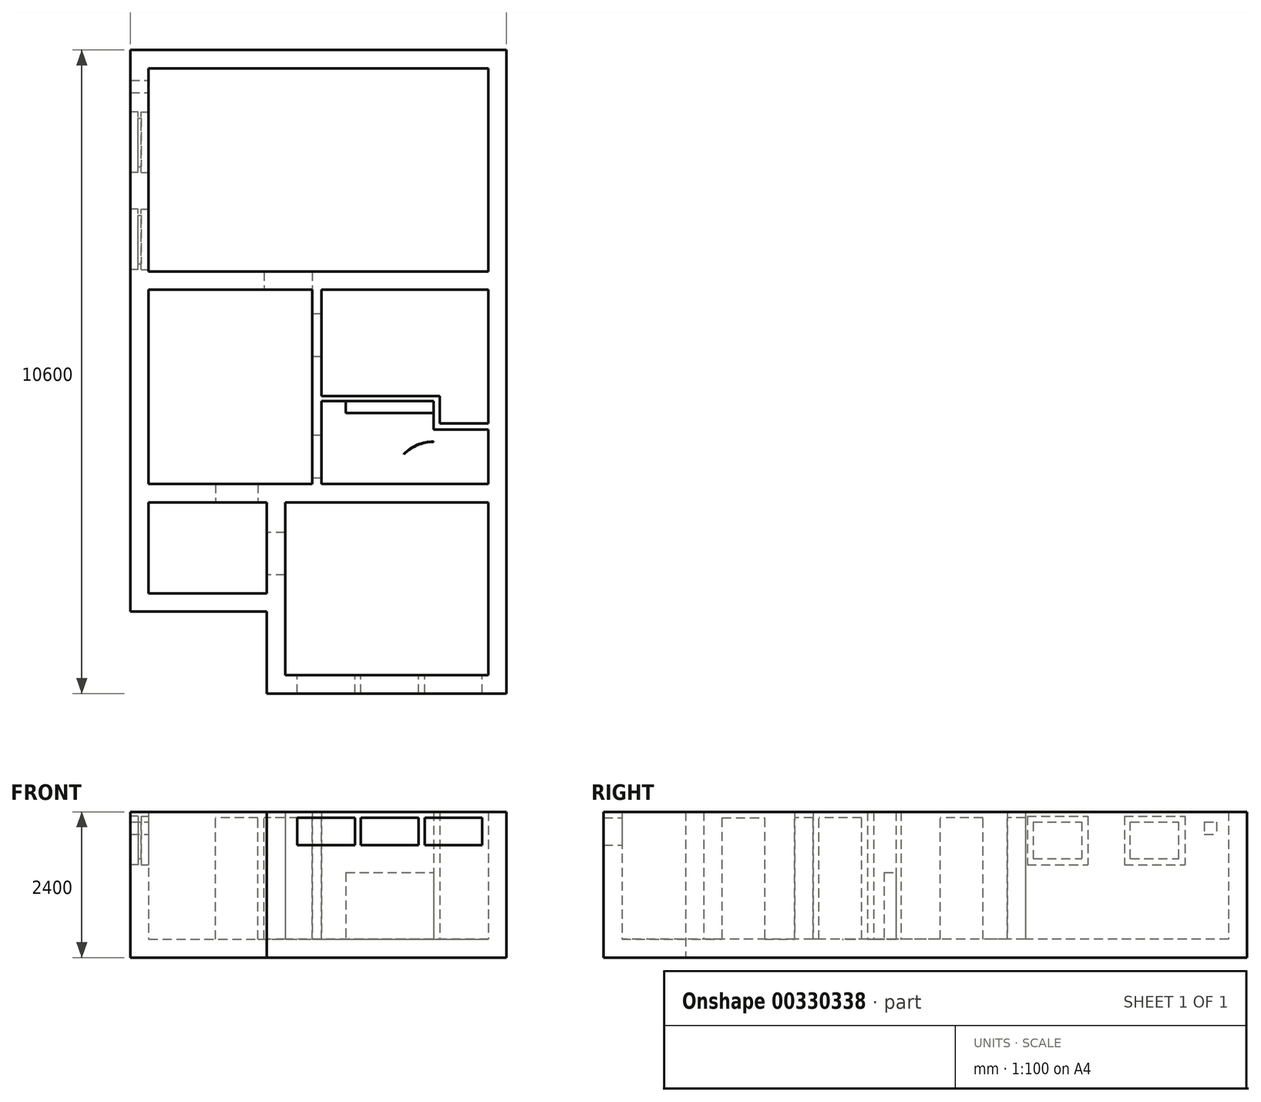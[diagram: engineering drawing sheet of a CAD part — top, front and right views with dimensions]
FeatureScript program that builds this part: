
annotation { "Feature Type Name" : "Feature", "Feature Type Description" : "" }
export const myFeature = defineFeature(function(context is Context, id is Id, definition is map)
    precondition{}
    {
        {
            var Q0;
            Q0=qCreatedBy(makeId("Top.planeOp"),FACE);
            var sketch = newSketch(context, id + "F0", { "sketchPlane" : qUnion([Q0])});
            skLineSegment(sketch, "E0.bottom", {"start": v(0, 0) * mm, "end": v(5600, 0) * mm});
            skLineSegment(sketch, "E0.top", {"start": v(0, -8650) * mm, "end": v(1950, -8650) * mm});
            skLineSegment(sketch, "E0.left", {"start": v(0, 0) * mm, "end": v(0, -3350) * mm});
            skLineSegment(sketch, "E0.right", {"start": v(5600, 0) * mm, "end": v(5600, -3350) * mm});
            skLineSegment(sketch, "E1", {"start": v(0, -3650) * mm, "end": v(2700, -3650) * mm});
            skLineSegment(sketch, "E2", {"start": v(5600, -8650) * mm, "end": v(5600, -10000) * mm});
            skLineSegment(sketch, "E3", {"start": v(5600, -10000) * mm, "end": v(2250, -10000) * mm});
            skLineSegment(sketch, "E4", {"start": v(2250, -10000) * mm, "end": v(2250, -8650) * mm});
            skLineSegment(sketch, "E5", {"start": v(0, -7150) * mm, "end": v(1950, -7150) * mm});
            skLineSegment(sketch, "E6", {"start": v(2250, -8650) * mm, "end": v(2250, -7150) * mm});
            skLineSegment(sketch, "E7", {"start": v(0, -3350) * mm, "end": v(5600, -3350) * mm});
            skLineSegment(sketch, "E8", {"start": v(0, -6850) * mm, "end": v(2700, -6850) * mm});
            skLineSegment(sketch, "E9", {"start": v(1950, -7150) * mm, "end": v(1950, -8650) * mm});
            skLineSegment(sketch, "E10.bottom", {"start": v(5900, 300) * mm, "end": v(-300, 300) * mm});
            skLineSegment(sketch, "E10.top", {"start": v(5900, -10300) * mm, "end": v(1950, -10300) * mm});
            skLineSegment(sketch, "E10.left", {"start": v(5900, 300) * mm, "end": v(5900, -10300) * mm});
            skLineSegment(sketch, "E10.right", {"start": v(-300, 300) * mm, "end": v(-300, -8950) * mm});
            skLineSegment(sketch, "E11", {"start": v(-300, -8950) * mm, "end": v(1950, -8950) * mm});
            skLineSegment(sketch, "E12", {"start": v(1950, -8950) * mm, "end": v(1950, -10300) * mm});
            skLineSegment(sketch, "E13", {"start": v(2700, -3650) * mm, "end": v(2700, -6850) * mm});
            skLineSegment(sketch, "E14.trimOffspring", {"start": v(0, -3650) * mm, "end": v(0, -6850) * mm});
            skLineSegment(sketch, "E15.trimOffspring", {"start": v(2850, -3650) * mm, "end": v(5600, -3650) * mm});
            skLineSegment(sketch, "E16.trimOffspring", {"start": v(2850, -6850) * mm, "end": v(5600, -6850) * mm});
            skLineSegment(sketch, "E17.trimOffspring", {"start": v(2250, -7150) * mm, "end": v(5600, -7150) * mm});
            skLineSegment(sketch, "E18.trimOffspring", {"start": v(5600, -7150) * mm, "end": v(5600, -8650) * mm});
            skLineSegment(sketch, "E19.trimOffspring", {"start": v(0, -7150) * mm, "end": v(0, -8650) * mm});
            skLineSegment(sketch, "E20", {"start": v(5600, -3650) * mm, "end": v(5600, -5850) * mm});
            skLineSegment(sketch, "E21", {"start": v(2850, -3650) * mm, "end": v(2850, -5400) * mm});
            skLineSegment(sketch, "E22.bottom", {"start": v(5600, -5850) * mm, "end": v(4800, -5850) * mm});
            skLineSegment(sketch, "E22.top", {"start": v(5600, -5950) * mm, "end": v(4700, -5950) * mm});
            skLineSegment(sketch, "E23.trimOffspring", {"start": v(2850, -5480) * mm, "end": v(2850, -6850) * mm});
            skLineSegment(sketch, "E24.trimOffspring", {"start": v(5600, -5950) * mm, "end": v(5600, -6850) * mm});
            skLineSegment(sketch, "E25.top", {"start": v(2850, -5400) * mm, "end": v(4800, -5400) * mm});
            skLineSegment(sketch, "E26.top", {"start": v(2850, -5480) * mm, "end": v(4700, -5480) * mm});
            skLineSegment(sketch, "E26.right", {"start": v(4700, -5950) * mm, "end": v(4700, -5480) * mm});
            skLineSegment(sketch, "E27.right", {"start": v(4800, -5850) * mm, "end": v(4800, -5400) * mm});
            skSolve(sketch);
        }
        {
            var Q0;
            Q0=qSketchRegion(id+"F0",true);
            extrude(context, id + "F1", {"entities" : qUnion([Q0]), "depth" : 2100 * mm});
        }
        {
            var Q0;
            Q0=makeQuery(id+"F0.imprint","IMPRINT",FACE,{"disambiguationData":[TD([[makeQuery(id+"F0.imprint","IMPRINT",EDGE,{"derivedFrom":sQuery(id+"F0.wireOp",EDGE,"E0.bottom")}),1.0]])]});
            var sketch = newSketch(context, id + "F2", { "sketchPlane" : qUnion([Q0])});
            skLineSegment(sketch, "E28.0", {"start": v(-300, -8950) * mm, "end": v(1950, -8950) * mm});
            skLineSegment(sketch, "E29.0", {"start": v(-300, 300) * mm, "end": v(-300, -8950) * mm});
            skLineSegment(sketch, "E30.0", {"start": v(5900, 300) * mm, "end": v(-300, 300) * mm});
            skLineSegment(sketch, "E31.0", {"start": v(5900, 300) * mm, "end": v(5900, -10300) * mm});
            skLineSegment(sketch, "E32.0", {"start": v(5900, -10300) * mm, "end": v(1950, -10300) * mm});
            skLineSegment(sketch, "E33.0", {"start": v(1950, -8950) * mm, "end": v(1950, -10300) * mm});
            skSolve(sketch);
        }
        {
            var Q0;
            Q0=qSketchRegion(id+"F2",true);
            extrude(context, id + "F3", {"entities" : qUnion([Q0]), "operationType" : NewBodyOperationType.ADD, "oppositeDirection" : true, "depth" : 300 * mm});
        }
        {
            var Q0;
            Q0=makeQuery(id+"F1.opExtrude","SWEPT_FACE",FACE,{"disambiguationData":[OSD([sQuery(id+"F0.wireOp",EDGE,"E3")])]});
            var sketch = newSketch(context, id + "F4", { "sketchPlane" : qUnion([Q0])});
            skLineSegment(sketch, "E34.bottom", {"start": v(-5500, 2000) * mm, "end": v(-4550, 2000) * mm});
            skLineSegment(sketch, "E34.top", {"start": v(-5500, 1550) * mm, "end": v(-4550, 1550) * mm});
            skLineSegment(sketch, "E34.left", {"start": v(-5500, 2000) * mm, "end": v(-5500, 1550) * mm});
            skLineSegment(sketch, "E34.right", {"start": v(-4550, 2000) * mm, "end": v(-4550, 1550) * mm});
            skLineSegment(sketch, "E35.bottom", {"start": v(-4450, 2000) * mm, "end": v(-3500, 2000) * mm});
            skLineSegment(sketch, "E35.top", {"start": v(-4450, 1550) * mm, "end": v(-3500, 1550) * mm});
            skLineSegment(sketch, "E35.left", {"start": v(-4450, 2000) * mm, "end": v(-4450, 1550) * mm});
            skLineSegment(sketch, "E35.right", {"start": v(-3500, 2000) * mm, "end": v(-3500, 1550) * mm});
            skLineSegment(sketch, "E36.bottom", {"start": v(-3400, 2000) * mm, "end": v(-2450, 2000) * mm});
            skLineSegment(sketch, "E36.top", {"start": v(-3400, 1550) * mm, "end": v(-2450, 1550) * mm});
            skLineSegment(sketch, "E36.left", {"start": v(-3400, 2000) * mm, "end": v(-3400, 1550) * mm});
            skLineSegment(sketch, "E36.right", {"start": v(-2450, 2000) * mm, "end": v(-2450, 1550) * mm});
            skSolve(sketch);
        }
        {
            var Q0;
            Q0=qSketchRegion(id+"F4",true);
            extrude(context, id + "F5", {"entities" : qUnion([Q0]), "operationType" : NewBodyOperationType.REMOVE, "endBound" : BoundingType.UP_TO_NEXT, "oppositeDirection" : true, "depth" : 25 * mm});
        }
        {
            var Q0;
            Q0=makeQuery(id+"F1.opExtrude","SWEPT_FACE",FACE,{"disambiguationData":[OSD([sQuery(id+"F0.wireOp",EDGE,"E5")])]});
            var sketch = newSketch(context, id + "F6", { "sketchPlane" : qUnion([Q0])});
            skLineSegment(sketch, "E37.bottom", {"start": v(1800, 0) * mm, "end": v(1100, 0) * mm});
            skLineSegment(sketch, "E37.top", {"start": v(1800, 2000) * mm, "end": v(1100, 2000) * mm});
            skLineSegment(sketch, "E37.left", {"start": v(1800, 0) * mm, "end": v(1800, 2000) * mm});
            skLineSegment(sketch, "E37.right", {"start": v(1100, 0) * mm, "end": v(1100, 2000) * mm});
            skSolve(sketch);
        }
        {
            var Q0;
            Q0=qSketchRegion(id+"F6",true);
            extrude(context, id + "F7", {"entities" : qUnion([Q0]), "operationType" : NewBodyOperationType.REMOVE, "endBound" : BoundingType.UP_TO_NEXT, "oppositeDirection" : true, "depth" : 25 * mm});
        }
        {
            var Q0;
            Q0=makeQuery(id+"F1.opExtrude","SWEPT_FACE",FACE,{"disambiguationData":[OSD([sQuery(id+"F0.wireOp",EDGE,"E9")])]});
            var sketch = newSketch(context, id + "F8", { "sketchPlane" : qUnion([Q0])});
            skLineSegment(sketch, "E38.bottom", {"start": v(7650, 0) * mm, "end": v(8350, 0) * mm});
            skLineSegment(sketch, "E38.top", {"start": v(7650, 2000) * mm, "end": v(8350, 2000) * mm});
            skLineSegment(sketch, "E38.left", {"start": v(7650, 0) * mm, "end": v(7650, 2000) * mm});
            skLineSegment(sketch, "E38.right", {"start": v(8350, 0) * mm, "end": v(8350, 2000) * mm});
            skSolve(sketch);
        }
        {
            var Q0;
            Q0=qSketchRegion(id+"F8",true);
            extrude(context, id + "F9", {"entities" : qUnion([Q0]), "operationType" : NewBodyOperationType.REMOVE, "endBound" : BoundingType.UP_TO_NEXT, "oppositeDirection" : true, "depth" : 25 * mm});
        }
        {
            var Q0;
            Q0=makeQuery(id+"F1.opExtrude","SWEPT_FACE",FACE,{"disambiguationData":[OSD([sQuery(id+"F0.wireOp",EDGE,"E1")])]});
            var sketch = newSketch(context, id + "F10", { "sketchPlane" : qUnion([Q0])});
            skLineSegment(sketch, "E39.bottom", {"start": v(2700, 0) * mm, "end": v(1900, 0) * mm});
            skLineSegment(sketch, "E39.top", {"start": v(2700, 2000) * mm, "end": v(1900, 2000) * mm});
            skLineSegment(sketch, "E39.left", {"start": v(2700, 0) * mm, "end": v(2700, 2000) * mm});
            skLineSegment(sketch, "E39.right", {"start": v(1900, 0) * mm, "end": v(1900, 2000) * mm});
            skSolve(sketch);
        }
        {
            var Q0;
            Q0=qSketchRegion(id+"F10",true);
            extrude(context, id + "F11", {"entities" : qUnion([Q0]), "operationType" : NewBodyOperationType.REMOVE, "endBound" : BoundingType.UP_TO_NEXT, "oppositeDirection" : true, "depth" : 25 * mm});
        }
        {
            var Q0;
            Q0=makeQuery(id+"F1.opExtrude","SWEPT_FACE",FACE,{"disambiguationData":[OSD([sQuery(id+"F0.wireOp",EDGE,"E13")])]});
            var sketch = newSketch(context, id + "F12", { "sketchPlane" : qUnion([Q0])});
            skLineSegment(sketch, "E40.bottom", {"start": v(6050, 0) * mm, "end": v(6750, 0) * mm});
            skLineSegment(sketch, "E40.top", {"start": v(6050, 2000) * mm, "end": v(6750, 2000) * mm});
            skLineSegment(sketch, "E40.left", {"start": v(6050, 0) * mm, "end": v(6050, 2000) * mm});
            skLineSegment(sketch, "E40.right", {"start": v(6750, 0) * mm, "end": v(6750, 2000) * mm});
            skLineSegment(sketch, "E41.bottom", {"start": v(4050, 0) * mm, "end": v(4750, 0) * mm});
            skLineSegment(sketch, "E41.top", {"start": v(4050, 2000) * mm, "end": v(4750, 2000) * mm});
            skLineSegment(sketch, "E41.left", {"start": v(4050, 0) * mm, "end": v(4050, 2000) * mm});
            skLineSegment(sketch, "E41.right", {"start": v(4750, 0) * mm, "end": v(4750, 2000) * mm});
            skSolve(sketch);
        }
        {
            var Q0;
            Q0=qSketchRegion(id+"F12",true);
            extrude(context, id + "F13", {"entities" : qUnion([Q0]), "operationType" : NewBodyOperationType.REMOVE, "endBound" : BoundingType.UP_TO_NEXT, "oppositeDirection" : true, "depth" : 25 * mm});
        }
        {
            var Q0;
            Q0=makeQuery(id+"F1.opExtrude","SWEPT_FACE",FACE,{"disambiguationData":[OSD([sQuery(id+"F0.wireOp",EDGE,"E0.left")])]});
            var sketch = newSketch(context, id + "F14", { "sketchPlane" : qUnion([Q0])});
            skLineSegment(sketch, "E42.bottom", {"start": v(-3220, 1930) * mm, "end": v(-2420, 1930) * mm});
            skLineSegment(sketch, "E42.top", {"start": v(-3220, 1730) * mm, "end": v(-2420, 1730) * mm});
            skLineSegment(sketch, "E42.left", {"start": v(-3220, 1930) * mm, "end": v(-3220, 1730) * mm});
            skLineSegment(sketch, "E42.right", {"start": v(-2420, 1930) * mm, "end": v(-2420, 1730) * mm});
            skLineSegment(sketch, "E43.bottom", {"start": v(-400, 1930) * mm, "end": v(-200, 1930) * mm});
            skLineSegment(sketch, "E43.top", {"start": v(-400, 1730) * mm, "end": v(-200, 1730) * mm});
            skLineSegment(sketch, "E43.left", {"start": v(-400, 1930) * mm, "end": v(-400, 1730) * mm});
            skLineSegment(sketch, "E43.right", {"start": v(-200, 1930) * mm, "end": v(-200, 1730) * mm});
            skSolve(sketch);
        }
        {
            var Q0;
            Q0 = qSketchRegion(id + "F14", true);
            extrude(context, id + "F15", {"entities" : qUnion([Q0]), "operationType" : NewBodyOperationType.REMOVE, "endBound" : BoundingType.THROUGH_ALL, "oppositeDirection" : true, "depth" : 25 * mm});
        }
        {
            var Q0;
            Q0=makeQuery(id+"F1.opExtrude","SWEPT_FACE",FACE,{"disambiguationData":[OSD([sQuery(id+"F0.wireOp",EDGE,"E0.left")])]});
            var sketch = newSketch(context, id + "F16", { "sketchPlane" : qUnion([Q0])});
            skLineSegment(sketch, "E44.bottom", {"start": v(-3220, 1930) * mm, "end": v(-2420, 1930) * mm});
            skLineSegment(sketch, "E44.top", {"start": v(-3220, 1330) * mm, "end": v(-2420, 1330) * mm});
            skLineSegment(sketch, "E44.left", {"start": v(-3220, 1930) * mm, "end": v(-3220, 1330) * mm});
            skLineSegment(sketch, "E44.right", {"start": v(-2420, 1930) * mm, "end": v(-2420, 1330) * mm});
            skLineSegment(sketch, "E45.bottom", {"start": v(-1620, 1330) * mm, "end": v(-820, 1330) * mm});
            skLineSegment(sketch, "E45.top", {"start": v(-1620, 1930) * mm, "end": v(-820, 1930) * mm});
            skLineSegment(sketch, "E45.left", {"start": v(-1620, 1330) * mm, "end": v(-1620, 1930) * mm});
            skLineSegment(sketch, "E45.right", {"start": v(-820, 1330) * mm, "end": v(-820, 1930) * mm});
            skLineSegment(sketch, "E46.bottom", {"start": v(-400, 1930) * mm, "end": v(-200, 1930) * mm});
            skLineSegment(sketch, "E46.top", {"start": v(-400, 1730) * mm, "end": v(-200, 1730) * mm});
            skLineSegment(sketch, "E46.left", {"start": v(-400, 1930) * mm, "end": v(-400, 1730) * mm});
            skLineSegment(sketch, "E46.right", {"start": v(-200, 1930) * mm, "end": v(-200, 1730) * mm});
            skSolve(sketch);
        }
        {
            var Q0;
            Q0 = qSketchRegion(id + "F16", true);
            extrude(context, id + "F17", {"entities" : qUnion([Q0]), "operationType" : NewBodyOperationType.REMOVE, "endBound" : BoundingType.THROUGH_ALL, "oppositeDirection" : true, "depth" : 25 * mm});
        }
        {
            var Q0;
            Q0=makeQuery(id+"F1.opExtrude","SWEPT_FACE",FACE,{"disambiguationData":[OSD([sQuery(id+"F0.wireOp",EDGE,"E0.left")])]});
            var sketch = newSketch(context, id + "F18", { "sketchPlane" : qUnion([Q0])});
            skLineSegment(sketch, "E47.bottom", {"start": v(-3320, 2030) * mm, "end": v(-2320, 2030) * mm});
            skLineSegment(sketch, "E47.top", {"start": v(-3320, 1230) * mm, "end": v(-2320, 1230) * mm});
            skLineSegment(sketch, "E47.left", {"start": v(-3320, 2030) * mm, "end": v(-3320, 1230) * mm});
            skLineSegment(sketch, "E47.right", {"start": v(-2320, 2030) * mm, "end": v(-2320, 1230) * mm});
            skLineSegment(sketch, "E48.bottom", {"start": v(-1720, 2030) * mm, "end": v(-720, 2030) * mm});
            skLineSegment(sketch, "E48.top", {"start": v(-1720, 1230) * mm, "end": v(-720, 1230) * mm});
            skLineSegment(sketch, "E48.left", {"start": v(-1720, 2030) * mm, "end": v(-1720, 1230) * mm});
            skLineSegment(sketch, "E48.right", {"start": v(-720, 2030) * mm, "end": v(-720, 1230) * mm});
            skSolve(sketch);
        }
        {
            var Q0;
            Q0 = qSketchRegion(id + "F18", true);
            extrude(context, id + "F19", {"entities" : qUnion([Q0]), "operationType" : NewBodyOperationType.REMOVE, "oppositeDirection" : true, "depth" : 125 * mm});
        }
        {
            var Q0;
            Q0=makeQuery(id+"F3.boolean.opBoolean","MERGE",FACE,{"derivedFrom":[makeQuery(id+"F1.opExtrude","SWEPT_FACE",FACE,{"disambiguationData":[OSD([sQuery(id+"F0.wireOp",EDGE,"E10.right")])]}),makeQuery(id+"F3.opExtrude","SWEPT_FACE",FACE,{"disambiguationData":[OSD([sQuery(id+"F2.wireOp",EDGE,"E29.0")])]})]});
            var sketch = newSketch(context, id + "F20", { "sketchPlane" : qUnion([Q0])});
            skLineSegment(sketch, "E49.bottom", {"start": v(3320, 2030) * mm, "end": v(2320, 2030) * mm});
            skLineSegment(sketch, "E49.top", {"start": v(3320, 1230) * mm, "end": v(2320, 1230) * mm});
            skLineSegment(sketch, "E49.left", {"start": v(3320, 2030) * mm, "end": v(3320, 1230) * mm});
            skLineSegment(sketch, "E49.right", {"start": v(2320, 2030) * mm, "end": v(2320, 1230) * mm});
            skLineSegment(sketch, "E50.bottom", {"start": v(1720, 2030) * mm, "end": v(720, 2030) * mm});
            skLineSegment(sketch, "E50.top", {"start": v(1720, 1230) * mm, "end": v(720, 1230) * mm});
            skLineSegment(sketch, "E50.left", {"start": v(1720, 2030) * mm, "end": v(1720, 1230) * mm});
            skLineSegment(sketch, "E50.right", {"start": v(720, 2030) * mm, "end": v(720, 1230) * mm});
            skSolve(sketch);
        }
        {
            var Q0;
            Q0 = qSketchRegion(id + "F20", true);
            extrude(context, id + "F21", {"entities" : qUnion([Q0]), "operationType" : NewBodyOperationType.REMOVE, "oppositeDirection" : true, "depth" : 125 * mm});
        }
        {
            var Q0;
            {var subQ0=makeQuery(id+"F3.opExtrude","CAP_FACE",FACE,{"disambiguationData":[OSD([sQuery(id+"F2.wireOp",EDGE,"E28.0"),sQuery(id+"F2.wireOp",EDGE,"E29.0"),sQuery(id+"F2.wireOp",EDGE,"E30.0"),sQuery(id+"F2.wireOp",EDGE,"E31.0"),sQuery(id+"F2.wireOp",EDGE,"E32.0"),sQuery(id+"F2.wireOp",EDGE,"E33.0")])],"isStart":true});Q0=makeQuery(id+"F13.boolean.opBoolean","MERGE",FACE,{"derivedFrom":[makeQuery(id+"F3.boolean.opBoolean","SPLIT",FACE,{"disambiguationData":[TD([makeQuery(id+"F1.opExtrude","SWEPT_FACE",FACE,{"disambiguationData":[OSD([sQuery(id+"F0.wireOp",EDGE,"E15.trimOffspring")])]})])],"derivedFrom":subQ0}),makeQuery(id+"F3.boolean.opBoolean","SPLIT",FACE,{"disambiguationData":[TD([makeQuery(id+"F1.opExtrude","SWEPT_FACE",FACE,{"disambiguationData":[OSD([sQuery(id+"F0.wireOp",EDGE,"E16.trimOffspring")])]})])],"derivedFrom":subQ0}),makeQuery(id+"F11.boolean.opBoolean","MERGE",FACE,{"derivedFrom":[makeQuery(id+"F3.boolean.opBoolean","SPLIT",FACE,{"disambiguationData":[TD([makeQuery(id+"F1.opExtrude","SWEPT_FACE",FACE,{"disambiguationData":[OSD([sQuery(id+"F0.wireOp",EDGE,"E0.bottom")])]})])],"derivedFrom":subQ0}),makeQuery(id+"F9.boolean.opBoolean","MERGE",FACE,{"derivedFrom":[makeQuery(id+"F3.boolean.opBoolean","SPLIT",FACE,{"disambiguationData":[TD([makeQuery(id+"F1.opExtrude","SWEPT_FACE",FACE,{"disambiguationData":[OSD([sQuery(id+"F0.wireOp",EDGE,"E3")])]})])],"derivedFrom":subQ0}),makeQuery(id+"F7.boolean.opBoolean","MERGE",FACE,{"derivedFrom":[makeQuery(id+"F3.boolean.opBoolean","SPLIT",FACE,{"disambiguationData":[TD([makeQuery(id+"F1.opExtrude","SWEPT_FACE",FACE,{"disambiguationData":[OSD([sQuery(id+"F0.wireOp",EDGE,"E0.top")])]})])],"derivedFrom":subQ0}),makeQuery(id+"F3.boolean.opBoolean","SPLIT",FACE,{"disambiguationData":[TD([makeQuery(id+"F1.opExtrude","SWEPT_FACE",FACE,{"disambiguationData":[OSD([sQuery(id+"F0.wireOp",EDGE,"E1")])]})])],"derivedFrom":subQ0}),makeQuery(id+"F7.opExtrude","SWEPT_FACE",FACE,{"disambiguationData":[OSD([sQuery(id+"F6.wireOp",EDGE,"E37.bottom")])]})]}),makeQuery(id+"F9.opExtrude","SWEPT_FACE",FACE,{"disambiguationData":[OSD([sQuery(id+"F8.wireOp",EDGE,"E38.bottom")])]})]}),makeQuery(id+"F11.opExtrude","SWEPT_FACE",FACE,{"disambiguationData":[OSD([sQuery(id+"F10.wireOp",EDGE,"E39.bottom")])]})]}),makeQuery(id+"F13.opExtrude","SWEPT_FACE",FACE,{"disambiguationData":[OSD([sQuery(id+"F12.wireOp",EDGE,"E40.bottom")])]}),makeQuery(id+"F13.opExtrude","SWEPT_FACE",FACE,{"disambiguationData":[OSD([sQuery(id+"F12.wireOp",EDGE,"E41.bottom")])]})]});}
            var sketch = newSketch(context, id + "F22", { "sketchPlane" : qUnion([Q0])});
            skLineSegment(sketch, "E51.bottom", {"start": v(4700, -5680) * mm, "end": v(3250, -5680) * mm});
            skLineSegment(sketch, "E51.top", {"start": v(4700, -5480) * mm, "end": v(3250, -5480) * mm});
            skLineSegment(sketch, "E51.left", {"start": v(4700, -5680) * mm, "end": v(4700, -5480) * mm});
            skLineSegment(sketch, "E52", {"start": v(3250, -5480) * mm, "end": v(3250, -5680) * mm});
            skSolve(sketch);
        }
        {
            var Q0;
            Q0 = qSketchRegion(id + "F22", true);
            extrude(context, id + "F23", {"entities" : qUnion([Q0]), "operationType" : NewBodyOperationType.ADD, "offsetDistance" : 25 * mm, "depth" : 1100 * mm});
        }
        {
            var Q0;
            {var subQ0=makeQuery(id+"F3.opExtrude","CAP_FACE",FACE,{"disambiguationData":[OSD([sQuery(id+"F2.wireOp",EDGE,"E28.0"),sQuery(id+"F2.wireOp",EDGE,"E29.0"),sQuery(id+"F2.wireOp",EDGE,"E30.0"),sQuery(id+"F2.wireOp",EDGE,"E31.0"),sQuery(id+"F2.wireOp",EDGE,"E32.0"),sQuery(id+"F2.wireOp",EDGE,"E33.0")])],"isStart":true});Q0=makeQuery(id+"F13.boolean.opBoolean","MERGE",FACE,{"derivedFrom":[makeQuery(id+"F3.boolean.opBoolean","SPLIT",FACE,{"disambiguationData":[TD([makeQuery(id+"F1.opExtrude","SWEPT_FACE",FACE,{"disambiguationData":[OSD([sQuery(id+"F0.wireOp",EDGE,"E15.trimOffspring")])]})])],"derivedFrom":subQ0}),makeQuery(id+"F3.boolean.opBoolean","SPLIT",FACE,{"disambiguationData":[TD([makeQuery(id+"F1.opExtrude","SWEPT_FACE",FACE,{"disambiguationData":[OSD([sQuery(id+"F0.wireOp",EDGE,"E16.trimOffspring")])]})])],"derivedFrom":subQ0}),makeQuery(id+"F9.boolean.opBoolean","MERGE",FACE,{"derivedFrom":[makeQuery(id+"F3.boolean.opBoolean","SPLIT",FACE,{"disambiguationData":[TD([makeQuery(id+"F1.opExtrude","SWEPT_FACE",FACE,{"disambiguationData":[OSD([sQuery(id+"F0.wireOp",EDGE,"E3")])]})])],"derivedFrom":subQ0}),makeQuery(id+"F7.boolean.opBoolean","MERGE",FACE,{"derivedFrom":[makeQuery(id+"F3.boolean.opBoolean","SPLIT",FACE,{"disambiguationData":[TD([makeQuery(id+"F1.opExtrude","SWEPT_FACE",FACE,{"disambiguationData":[OSD([sQuery(id+"F0.wireOp",EDGE,"E0.bottom")])]})])],"derivedFrom":subQ0}),makeQuery(id+"F3.boolean.opBoolean","SPLIT",FACE,{"disambiguationData":[TD([makeQuery(id+"F1.opExtrude","SWEPT_FACE",FACE,{"disambiguationData":[OSD([sQuery(id+"F0.wireOp",EDGE,"E0.top")])]})])],"derivedFrom":subQ0}),makeQuery(id+"F7.opExtrude","SWEPT_FACE",FACE,{"disambiguationData":[OSD([sQuery(id+"F6.wireOp",EDGE,"E37.bottom")])]})]}),makeQuery(id+"F9.opExtrude","SWEPT_FACE",FACE,{"disambiguationData":[OSD([sQuery(id+"F8.wireOp",EDGE,"E38.bottom")])]})]}),makeQuery(id+"F13.opExtrude","SWEPT_FACE",FACE,{"disambiguationData":[OSD([sQuery(id+"F12.wireOp",EDGE,"E40.bottom")])]}),makeQuery(id+"F13.opExtrude","SWEPT_FACE",FACE,{"disambiguationData":[OSD([sQuery(id+"F12.wireOp",EDGE,"E41.bottom")])]})]});}
            var sketch = newSketch(context, id + "F24", { "sketchPlane" : qUnion([Q0])});
            skLineSegment(sketch, "E53", {"start": v(4700, -6850) * mm, "end": v(4205.03, -6355.03) * mm, "construction": true});
            skArc(sketch, "E54", {"start": v(4205.03, -6355.03) * mm, "mid": v(4432.12, -6203.28) * mm, "end": v(4700, -6150) * mm});
            skArc(sketch, "E55.0", {"start": v(4208.56, -6358.56) * mm, "mid": v(4434.04, -6207.9) * mm, "end": v(4700, -6155) * mm});
            skLineSegment(sketch, "E56", {"start": v(4700, -6150) * mm, "end": v(4700, -6155) * mm});
            skLineSegment(sketch, "E57", {"start": v(4208.56, -6358.56) * mm, "end": v(4205.03, -6355.03) * mm});
            skSolve(sketch);
        }
        {
            var Q0;
            Q0 = qSketchRegion(id + "F24", true);
            extrude(context, id + "F25", {"entities" : qUnion([Q0]), "operationType" : NewBodyOperationType.REMOVE, "oppositeDirection" : true, "depth" : 5 * mm, "offsetDistance" : 25 * mm});
        }
    });
